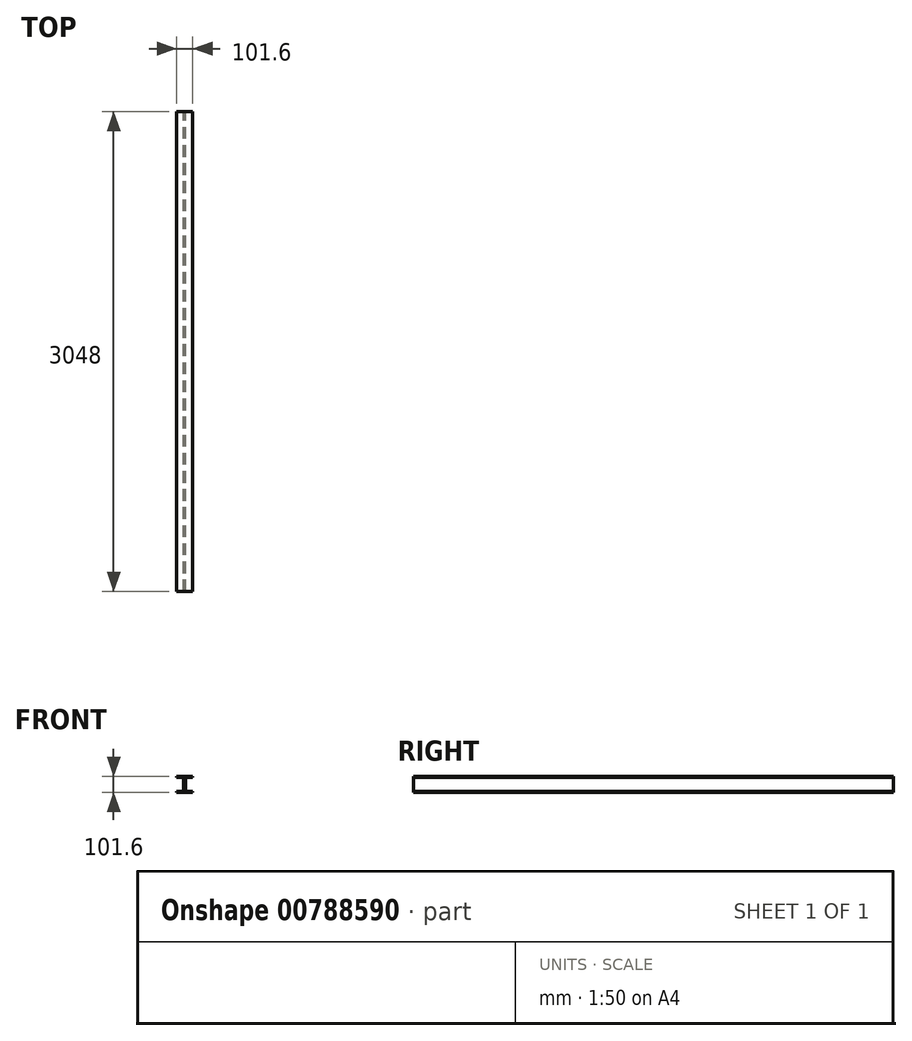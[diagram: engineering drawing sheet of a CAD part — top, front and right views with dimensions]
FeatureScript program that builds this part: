
annotation { "Feature Type Name" : "Feature", "Feature Type Description" : "" }
export const myFeature = defineFeature(function(context is Context, id is Id, definition is map)
    precondition{}
    {
        {
            var Q0;
            Q0=qCreatedBy(makeId("Front.planeOp"),FACE);
            var sketch = newSketch(context, id + "F0", { "sketchPlane" : qUnion([Q0])});
            skPoint(sketch, "E0", {"position": v(0, 0) * mm});
            skLineSegment(sketch, "E1", {"start": v(0, 0) * mm, "end": v(0, 101.6) * mm});
            skLineSegment(sketch, "E2", {"start": v(0, 101.6) * mm, "end": v(101.6, 101.6) * mm});
            skLineSegment(sketch, "E3", {"start": v(101.6, 101.6) * mm, "end": v(101.6, 0) * mm});
            skLineSegment(sketch, "E4", {"start": v(101.6, 0) * mm, "end": v(0, 0) * mm});
            skLineSegment(sketch, "E5", {"start": v(50.8, 101.6) * mm, "end": v(50.8, 0) * mm});
            skLineSegment(sketch, "E6", {"start": v(0, 101.6) * mm, "end": v(0, 95.25) * mm});
            skLineSegment(sketch, "E7", {"start": v(0, 95.25) * mm, "end": v(101.6, 95.25) * mm});
            skLineSegment(sketch, "E8", {"start": v(101.6, 95.25) * mm, "end": v(101.6, 101.6) * mm});
            skLineSegment(sketch, "E9.bottom", {"start": v(0, 0) * mm, "end": v(101.6, 0) * mm});
            skLineSegment(sketch, "E9.top", {"start": v(0, 6.35) * mm, "end": v(101.6, 6.35) * mm});
            skLineSegment(sketch, "E9.left", {"start": v(0, 0) * mm, "end": v(0, 6.35) * mm});
            skLineSegment(sketch, "E9.right", {"start": v(101.6, 0) * mm, "end": v(101.6, 6.35) * mm});
            skLineSegment(sketch, "E10.bottom", {"start": v(50.8, 101.6) * mm, "end": v(57.15, 101.6) * mm});
            skLineSegment(sketch, "E10.top", {"start": v(50.8, 6.35) * mm, "end": v(57.15, 6.35) * mm});
            skLineSegment(sketch, "E10.left", {"start": v(50.8, 101.6) * mm, "end": v(50.8, 6.35) * mm});
            skLineSegment(sketch, "E10.right", {"start": v(57.15, 101.6) * mm, "end": v(57.15, 6.35) * mm});
            skLineSegment(sketch, "E11.bottom", {"start": v(50.8, 101.6) * mm, "end": v(44.45, 101.6) * mm});
            skLineSegment(sketch, "E11.top", {"start": v(50.8, 6.35) * mm, "end": v(44.45, 6.35) * mm});
            skLineSegment(sketch, "E11.right", {"start": v(44.45, 101.6) * mm, "end": v(44.45, 6.35) * mm});
            skSolve(sketch);
        }
        {
            var Q0;
            {var subQ0=sQuery(id+"F0.wireOp",EDGE,"E2");var subQ1=sQuery(id+"F0.wireOp",EDGE,"E1");var subQ2=makeQuery(id+"F0.imprint","INTERSECT",VERTEX,{"derivedFrom":[subQ1,subQ0]});Q0=makeQuery(id+"F0.imprint","IMPRINT",FACE,{"disambiguationData":[TD([[makeQuery(id+"F0.imprint","IMPRINT",EDGE,{"disambiguationData":[TD([[subQ2,1.0]])],"derivedFrom":subQ1}),-1.0]])]});}
            var Q1;
            {var subQ0=sQuery(id+"F0.wireOp",EDGE,"E11.right");var subQ1=sQuery(id+"F0.wireOp",EDGE,"E2");var subQ2=makeQuery(id+"F0.imprint","INTERSECT",VERTEX,{"derivedFrom":[subQ1,subQ0]});Q1=makeQuery(id+"F0.imprint","IMPRINT",FACE,{"disambiguationData":[TD([[makeQuery(id+"F0.imprint","IMPRINT",EDGE,{"disambiguationData":[TD([[subQ2,-1.0]])],"derivedFrom":subQ1}),-1.0]])]});}
            var Q2;
            {var subQ0=sQuery(id+"F0.wireOp",EDGE,"E10.right");var subQ1=sQuery(id+"F0.wireOp",EDGE,"E2");var subQ2=makeQuery(id+"F0.imprint","INTERSECT",VERTEX,{"derivedFrom":[subQ1,subQ0]});Q2=makeQuery(id+"F0.imprint","IMPRINT",FACE,{"disambiguationData":[TD([[makeQuery(id+"F0.imprint","IMPRINT",EDGE,{"disambiguationData":[TD([[subQ2,1.0]])],"derivedFrom":subQ1}),-1.0]])]});}
            var Q3;
            {var subQ0=sQuery(id+"F0.wireOp",EDGE,"E10.right");var subQ1=sQuery(id+"F0.wireOp",EDGE,"E2");var subQ2=makeQuery(id+"F0.imprint","INTERSECT",VERTEX,{"derivedFrom":[subQ1,subQ0]});Q3=makeQuery(id+"F0.imprint","IMPRINT",FACE,{"disambiguationData":[TD([[makeQuery(id+"F0.imprint","IMPRINT",EDGE,{"disambiguationData":[TD([[subQ2,-1.0]])],"derivedFrom":subQ1}),-1.0]])]});}
            var Q4;
            {var subQ0=sQuery(id+"F0.wireOp",EDGE,"E7");var subQ1=sQuery(id+"F0.wireOp",EDGE,"E5");var subQ2=makeQuery(id+"F0.imprint","INTERSECT",VERTEX,{"derivedFrom":[subQ1,subQ0]});Q4=makeQuery(id+"F0.imprint","IMPRINT",FACE,{"disambiguationData":[TD([[makeQuery(id+"F0.imprint","IMPRINT",EDGE,{"disambiguationData":[TD([[subQ2,-1.0]])],"derivedFrom":subQ1}),1.0]])]});}
            var Q5;
            {var subQ0=sQuery(id+"F0.wireOp",EDGE,"E7");var subQ1=sQuery(id+"F0.wireOp",EDGE,"E5");var subQ2=makeQuery(id+"F0.imprint","INTERSECT",VERTEX,{"derivedFrom":[subQ1,subQ0]});Q5=makeQuery(id+"F0.imprint","IMPRINT",FACE,{"disambiguationData":[TD([[makeQuery(id+"F0.imprint","IMPRINT",EDGE,{"disambiguationData":[TD([[subQ2,-1.0]])],"derivedFrom":subQ1}),-1.0]])]});}
            var Q6;
            {var subQ0=sQuery(id+"F0.wireOp",EDGE,"E9.top");var subQ1=sQuery(id+"F0.wireOp",EDGE,"E1");var subQ2=makeQuery(id+"F0.imprint","INTERSECT",VERTEX,{"derivedFrom":[subQ1,subQ0]});Q6=makeQuery(id+"F0.imprint","IMPRINT",FACE,{"disambiguationData":[TD([[makeQuery(id+"F0.imprint","IMPRINT",EDGE,{"disambiguationData":[TD([[subQ2,1.0]])],"derivedFrom":subQ1}),-1.0]])]});}
            var Q7;
            {var subQ2=sQuery(id+"F0.wireOp",EDGE,"E3");var subQ4=sQuery(id+"F0.wireOp",EDGE,"E4");var subQ5=makeQuery(id+"F0.imprint","INTERSECT",VERTEX,{"derivedFrom":[subQ2,subQ4]});Q7=makeQuery(id+"F0.imprint","IMPRINT",FACE,{"disambiguationData":[TD([[makeQuery(id+"F0.imprint","IMPRINT",EDGE,{"disambiguationData":[TD([[subQ5,1.0]])],"derivedFrom":subQ2}),-1.0]])]});}
            extrude(context, id + "F1", {"entities" : qUnion([Q0, Q1, Q2, Q3, Q4, Q5, Q6, Q7]), "depth" : 3048 * mm, "offsetDistance" : 25.4 * mm});
        }
    });
